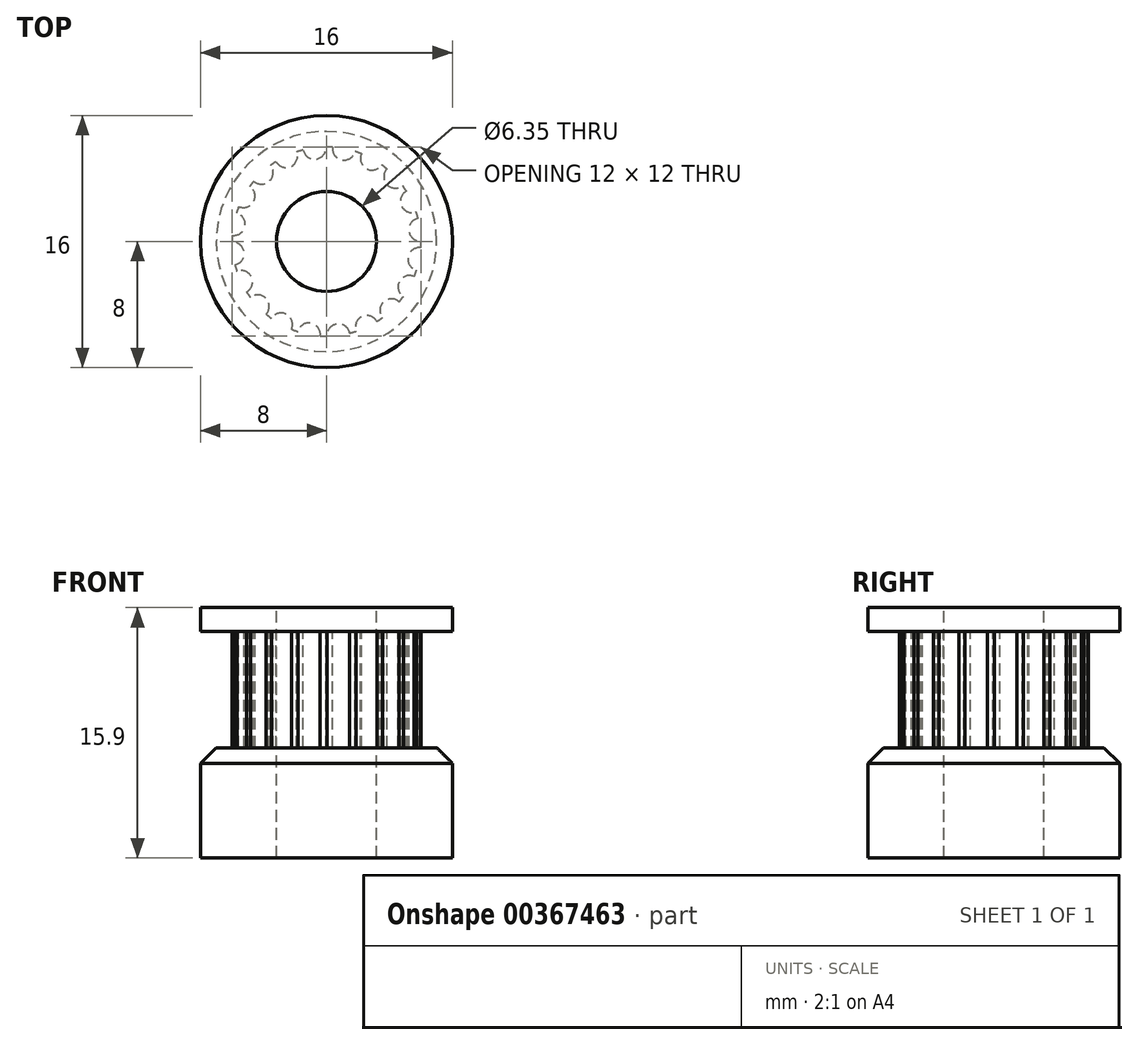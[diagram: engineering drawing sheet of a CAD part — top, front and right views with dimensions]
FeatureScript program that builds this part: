
annotation { "Feature Type Name" : "Feature", "Feature Type Description" : "" }
export const myFeature = defineFeature(function(context is Context, id is Id, definition is map)
    precondition{}
    {
        {
            var Q0;
            Q0=qCreatedBy(makeId("Top.planeOp"),FACE);
            var sketch = newSketch(context, id + "F0", { "sketchPlane" : qUnion([Q0])});
            skCircle(sketch, "E0", {"center": v(0, 0) * mm, "radius": 8 * mm});
            skSolve(sketch);
        }
        {
            var Q0;
            Q0=qSketchRegion(id+"F0",true);
            extrude(context, id + "F1", {"entities" : qUnion([Q0]), "depth" : 7 * mm});
        }
        {
            var Q0;
            Q0=makeQuery(id+"F1.opExtrude","CAP_FACE",FACE,{"disambiguationData":[OSD([sQuery(id+"F0.wireOp",EDGE,"E0")])],"isStart":false});
            var sketch = newSketch(context, id + "F2", { "sketchPlane" : qUnion([Q0])});
            skCircle(sketch, "E1", {"center": v(0, 0) * mm, "radius": 6 * mm});
            skSolve(sketch);
        }
        {
            var Q0;
            Q0=qSketchRegion(id+"F2",true);
            extrude(context, id + "F3", {"entities" : qUnion([Q0]), "operationType" : NewBodyOperationType.ADD, "depth" : 7.4 * mm});
        }
        {
            var Q0;
            Q0=makeQuery(id+"F1.opExtrude","CAP_EDGE",EDGE,{"disambiguationData":[OSD([sQuery(id+"F0.wireOp",EDGE,"E0")])],"isStart":false});
            chamfer(context, id + "F4", {"entities" : qUnion([Q0]), "width" : 1 * mm, "tangentPropagation" : true});
        }
        {
            var Q0;
            Q0=makeQuery(id+"F3.opExtrude","CAP_FACE",FACE,{"disambiguationData":[OSD([sQuery(id+"F2.wireOp",EDGE,"E1")])],"isStart":false});
            var sketch = newSketch(context, id + "F5", { "sketchPlane" : qUnion([Q0])});
            skCircle(sketch, "E2", {"center": v(0, 0) * mm, "radius": 8 * mm});
            skSolve(sketch);
        }
        {
            var Q0;
            Q0=qSketchRegion(id+"F5",true);
            extrude(context, id + "F6", {"entities" : qUnion([Q0]), "operationType" : NewBodyOperationType.ADD, "depth" : 1.5 * mm});
        }
        {
            var Q0;
            Q0=makeQuery(id+"F6.opExtrude","CAP_FACE",FACE,{"disambiguationData":[OSD([sQuery(id+"F5.wireOp",EDGE,"E2")])],"isStart":true});
            var sketch = newSketch(context, id + "F7", { "sketchPlane" : qUnion([Q0])});
            skCircle(sketch, "E3", {"center": v(-5.42, 2.56) * mm, "radius": 0.72 * mm});
            skCircle(sketch, "E4.1.0", {"center": v(-5.95, 0.76) * mm, "radius": 0.72 * mm});
            skCircle(sketch, "E4.2.0", {"center": v(-5.9, -1.11) * mm, "radius": 0.72 * mm});
            skCircle(sketch, "E4.3.0", {"center": v(-5.26, -2.88) * mm, "radius": 0.72 * mm});
            skCircle(sketch, "E4.4.0", {"center": v(-4.12, -4.37) * mm, "radius": 0.72 * mm});
            skCircle(sketch, "E4.5.0", {"center": v(-2.56, -5.42) * mm, "radius": 0.72 * mm});
            skCircle(sketch, "E4.6.0", {"center": v(-0.76, -5.95) * mm, "radius": 0.72 * mm});
            skCircle(sketch, "E4.7.0", {"center": v(1.11, -5.9) * mm, "radius": 0.72 * mm});
            skCircle(sketch, "E4.8.0", {"center": v(2.88, -5.26) * mm, "radius": 0.72 * mm});
            skCircle(sketch, "E4.9.0", {"center": v(4.37, -4.12) * mm, "radius": 0.72 * mm});
            skCircle(sketch, "E4.10.0", {"center": v(5.42, -2.56) * mm, "radius": 0.72 * mm});
            skCircle(sketch, "E4.11.0", {"center": v(5.95, -0.76) * mm, "radius": 0.72 * mm});
            skCircle(sketch, "E4.12.0", {"center": v(5.9, 1.11) * mm, "radius": 0.72 * mm});
            skCircle(sketch, "E4.13.0", {"center": v(5.26, 2.88) * mm, "radius": 0.72 * mm});
            skCircle(sketch, "E4.14.0", {"center": v(4.12, 4.37) * mm, "radius": 0.72 * mm});
            skCircle(sketch, "E4.15.0", {"center": v(2.56, 5.42) * mm, "radius": 0.72 * mm});
            skCircle(sketch, "E4.16.0", {"center": v(0.76, 5.95) * mm, "radius": 0.72 * mm});
            skCircle(sketch, "E4.17.0", {"center": v(-1.11, 5.9) * mm, "radius": 0.72 * mm});
            skCircle(sketch, "E4.18.0", {"center": v(-2.88, 5.26) * mm, "radius": 0.72 * mm});
            skCircle(sketch, "E4.19.0", {"center": v(-4.37, 4.12) * mm, "radius": 0.72 * mm});
            skPoint(sketch, "E4.center", {"position": v(0, 0) * mm});
            skSolve(sketch);
        }
        {
            var Q0;
            Q0=qSketchRegion(id+"F7",true);
            extrude(context, id + "F8", {"entities" : qUnion([Q0]), "operationType" : NewBodyOperationType.REMOVE, "depth" : 7.4 * mm});
        }
        {
            var Q0;
            Q0=makeQuery(id+"F6.opExtrude","CAP_FACE",FACE,{"disambiguationData":[OSD([sQuery(id+"F5.wireOp",EDGE,"E2")])],"isStart":false});
            var sketch = newSketch(context, id + "F9", { "sketchPlane" : qUnion([Q0])});
            skPoint(sketch, "E5", {"position": v(0, 0) * mm});
            skSolve(sketch);
        }
        {
            var Q0;
            Q0=sQuery(id+"F9.wireOp",VERTEX,"E5");
            var Q1;
            Q1=makeQuery(id+"F1.opExtrude","SWEPT_BODY",BODY,{"disambiguationData":[OSD([sQuery(id+"F0.wireOp",EDGE,"E0")])]});
            hole(context, id + "F10", {"style" : HoleStyle.SIMPLE, "endStyle" : HoleEndStyle.THROUGH, "holeDiameter" : 6.35 * mm, "locations" : qUnion([Q0]), "scope" : qUnion([Q1]), "isTappedThrough" : true});
        }
    });
